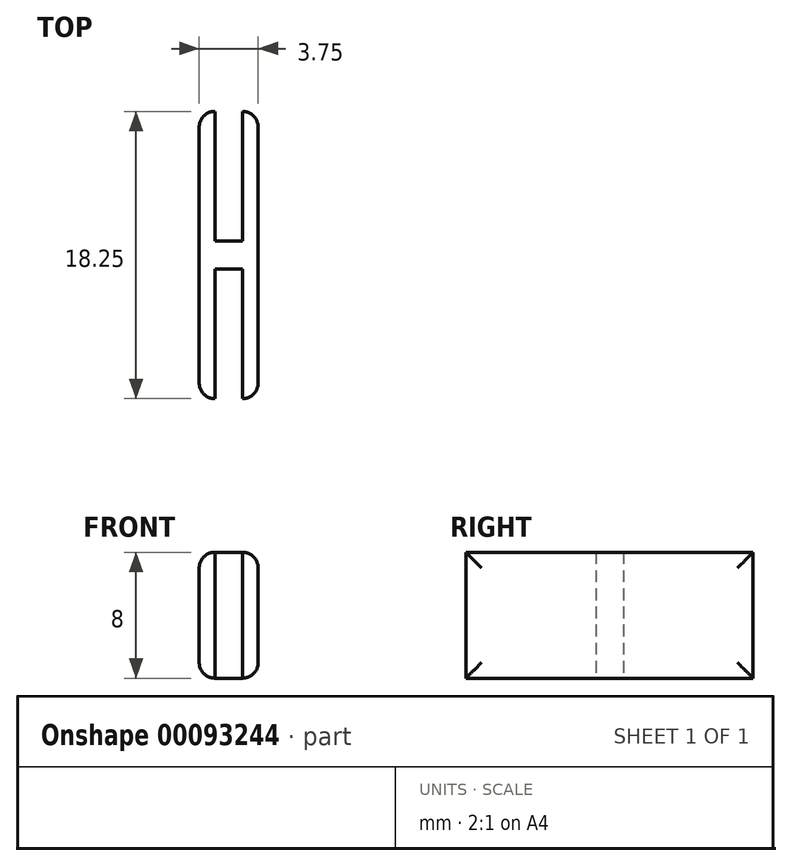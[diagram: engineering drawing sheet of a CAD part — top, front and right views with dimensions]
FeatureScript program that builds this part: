
annotation { "Feature Type Name" : "Feature", "Feature Type Description" : "" }
export const myFeature = defineFeature(function(context is Context, id is Id, definition is map)
    precondition{}
    {
        {
            var Q0;
            Q0=qCreatedBy(makeId("Top.planeOp"),FACE);
            var sketch = newSketch(context, id + "F0", { "sketchPlane" : qUnion([Q0])});
            skLineSegment(sketch, "E0.top", {"start": v(20.55, -18.35) * mm, "end": v(22.3, -18.35) * mm});
            skLineSegment(sketch, "E1.top", {"start": v(22.3, -8.35) * mm, "end": v(23.3, -8.35) * mm});
            skLineSegment(sketch, "E1.left", {"start": v(22.3, -16.6) * mm, "end": v(22.3, -8.35) * mm});
            skLineSegment(sketch, "E1.right", {"start": v(23.3, -18.35) * mm, "end": v(23.3, -8.35) * mm});
            skLineSegment(sketch, "E2.top", {"start": v(20.55, -8.35) * mm, "end": v(19.55, -8.35) * mm});
            skLineSegment(sketch, "E2.left", {"start": v(20.55, -16.6) * mm, "end": v(20.55, -8.35) * mm});
            skLineSegment(sketch, "E2.right", {"start": v(19.55, -18.35) * mm, "end": v(19.55, -8.35) * mm});
            skLineSegment(sketch, "E3.top", {"start": v(20.55, -16.6) * mm, "end": v(22.3, -16.6) * mm});
            skLineSegment(sketch, "E4.top", {"start": v(19.55, -26.6) * mm, "end": v(20.55, -26.6) * mm});
            skLineSegment(sketch, "E4.left", {"start": v(19.55, -18.35) * mm, "end": v(19.55, -26.6) * mm});
            skLineSegment(sketch, "E4.right", {"start": v(20.55, -18.35) * mm, "end": v(20.55, -26.6) * mm});
            skLineSegment(sketch, "E5.top", {"start": v(22.3, -26.6) * mm, "end": v(23.3, -26.6) * mm});
            skLineSegment(sketch, "E5.left", {"start": v(22.3, -18.35) * mm, "end": v(22.3, -26.6) * mm});
            skLineSegment(sketch, "E5.right", {"start": v(23.3, -18.35) * mm, "end": v(23.3, -26.6) * mm});
            skLineSegment(sketch, "E6.trimOffspring", {"start": v(23.3, -18.35) * mm, "end": v(27.4, -18.35) * mm});
            skSolve(sketch);
        }
        {
            var Q0;
            Q0=makeQuery(id+"F0.imprint","IMPRINT",FACE,{"disambiguationData":[TD([[makeQuery(id+"F0.imprint","IMPRINT",EDGE,{"derivedFrom":sQuery(id+"F0.wireOp",EDGE,"E0.top")}),1.0]])]});
            extrude(context, id + "F1", {"entities" : qUnion([Q0]), "depth" : 8 * mm});
        }
        {
            var Q0;
            Q0=makeQuery(id+"F1.opExtrude","SWEPT_EDGE",EDGE,{"disambiguationData":[OSD([sQuery(id+"F0.wireOp",EDGE,"E5.top"),sQuery(id+"F0.wireOp",EDGE,"E5.right")])]});
            var Q1;
            Q1=makeQuery(id+"F1.opExtrude","CAP_EDGE",EDGE,{"disambiguationData":[OSD([sQuery(id+"F0.wireOp",EDGE,"E1.right"),sQuery(id+"F0.wireOp",EDGE,"E5.right")])],"isStart":false});
            var Q2;
            Q2=makeQuery(id+"F1.opExtrude","SWEPT_EDGE",EDGE,{"disambiguationData":[OSD([sQuery(id+"F0.wireOp",EDGE,"E1.top"),sQuery(id+"F0.wireOp",EDGE,"E1.right")])]});
            var Q3;
            Q3=makeQuery(id+"F1.opExtrude","CAP_EDGE",EDGE,{"disambiguationData":[OSD([sQuery(id+"F0.wireOp",EDGE,"E1.right"),sQuery(id+"F0.wireOp",EDGE,"E5.right")])],"isStart":true});
            var Q4;
            Q4=makeQuery(id+"F1.opExtrude","SWEPT_EDGE",EDGE,{"disambiguationData":[OSD([sQuery(id+"F0.wireOp",EDGE,"E4.top"),sQuery(id+"F0.wireOp",EDGE,"E4.left")])]});
            var Q5;
            Q5=makeQuery(id+"F1.opExtrude","CAP_EDGE",EDGE,{"disambiguationData":[OSD([sQuery(id+"F0.wireOp",EDGE,"E2.right"),sQuery(id+"F0.wireOp",EDGE,"E4.left")])],"isStart":false});
            var Q6;
            Q6=makeQuery(id+"F1.opExtrude","SWEPT_EDGE",EDGE,{"disambiguationData":[OSD([sQuery(id+"F0.wireOp",EDGE,"E2.top"),sQuery(id+"F0.wireOp",EDGE,"E2.right")])]});
            var Q7;
            Q7=makeQuery(id+"F1.opExtrude","CAP_EDGE",EDGE,{"disambiguationData":[OSD([sQuery(id+"F0.wireOp",EDGE,"E2.right"),sQuery(id+"F0.wireOp",EDGE,"E4.left")])],"isStart":true});
            fillet(context, id + "F2", {"entities" : qUnion([Q0, Q1, Q2, Q3, Q4, Q5, Q6, Q7]), "radius" : 1 * mm, "tangentPropagation" : true, "allowEdgeOverflow" : false});
        }
    });
